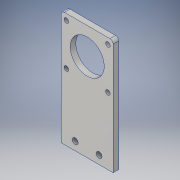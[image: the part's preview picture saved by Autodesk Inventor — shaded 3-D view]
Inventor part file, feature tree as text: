
AUTODESK INVENTOR PART (.ipt)
format: ipt  version: 2016 (Build 200138000, 138)  size: 143,360 bytes
history: native  units: in
note: dims shown in document units (in); Inventor stores cm internally (conversion verified against a paired STEP export)
features: extrude x4, sketch x4, fillet x1
ambient origin geometry x8: Origin, YZ Plane, XZ Plane, XY Plane, X Axis, Y Axis, Z Axis, Center Point
bodies: Solid1 (feature_tree)
feature tree (9):
  extrude  "Stock Bar"  Depth=5.115in
  fillet  "Round Edges"  Radius=0.25in
  extrude  "Motor Hole"  Depth=0.25in TaperAngle=0.0deg
  extrude  "Motor Mounting Holes"  Depth=0.7874in
  extrude  "Motor Support Mounting Holes"  Depth=0.142in
  sketch  "Sketch1"  dims[d0=2.318in d1=5.115in d2=0.25in d3=0.0in]
  sketch  "Sketch2"  dims[d4=1.52in d8=0.25in d9=0.0in]
  sketch  "Sketch3"  dims[d10=0.205in d13=0.7874in d15=1.856in d16=0.7874in d18=1.856in]
  sketch  "Sketch4"  dims[d21=0.25in d22=0.0in d23=0.142in d24=0.26in d25=0.26in d26=0.375in d27=0.375in d28=0.625in d29=0.625in d30=1.0in d31=0.0in d32=3.915in d33=4.843in d34=0.229in]
